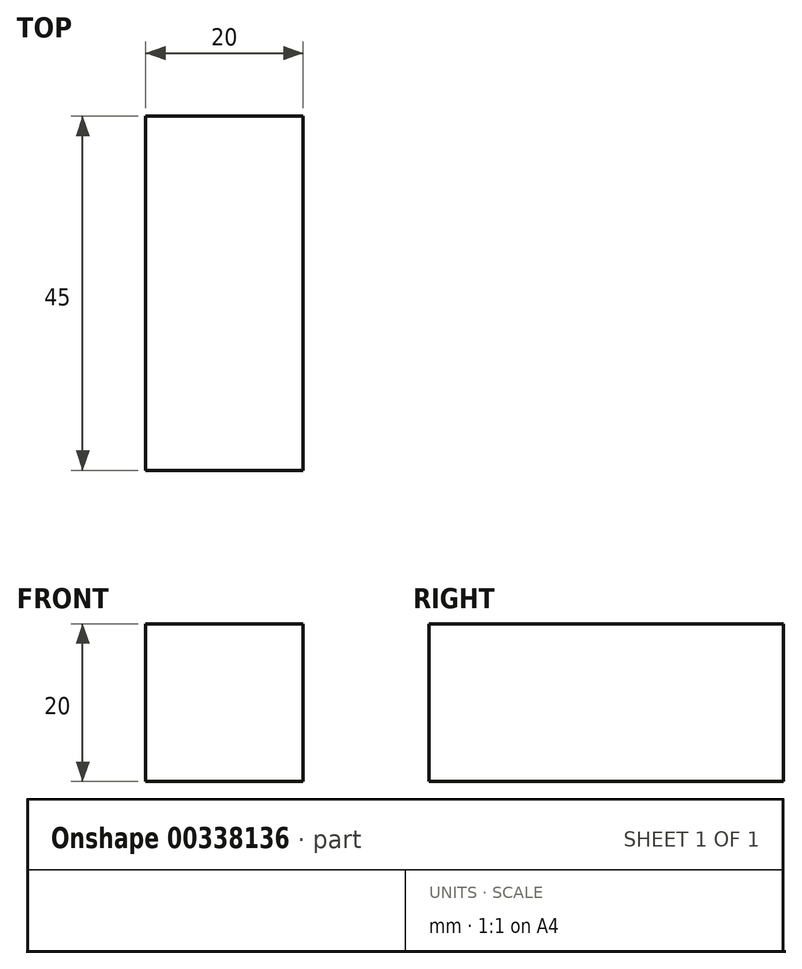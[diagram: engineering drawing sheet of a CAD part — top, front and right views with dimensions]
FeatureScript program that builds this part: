
annotation { "Feature Type Name" : "Feature", "Feature Type Description" : "" }
export const myFeature = defineFeature(function(context is Context, id is Id, definition is map)
    precondition{}
    {
        {
            var Q0;
            Q0=qCreatedBy(makeId("Front.planeOp"),FACE);
            var sketch = newSketch(context, id + "F0", { "sketchPlane" : qUnion([Q0])});
            skLineSegment(sketch, "E0.bottom", {"start": v(10, 10) * mm, "end": v(-10, 10) * mm});
            skLineSegment(sketch, "E0.top", {"start": v(10, -10) * mm, "end": v(-10, -10) * mm});
            skLineSegment(sketch, "E0.left", {"start": v(10, 10) * mm, "end": v(10, -10) * mm});
            skLineSegment(sketch, "E0.right", {"start": v(-10, 10) * mm, "end": v(-10, -10) * mm});
            skPoint(sketch, "E0.middle", {"position": v(0, 0) * mm});
            skSolve(sketch);
        }
        {
            var Q0;
            Q0=makeQuery(id+"F0.imprint","IMPRINT",FACE,{"disambiguationData":[TD([[makeQuery(id+"F0.imprint","IMPRINT",EDGE,{"derivedFrom":sQuery(id+"F0.wireOp",EDGE,"E0.bottom")}),1.0]])]});
            extrude(context, id + "F1", {"entities" : qUnion([Q0]), "depth" : 45 * mm});
        }
    });
